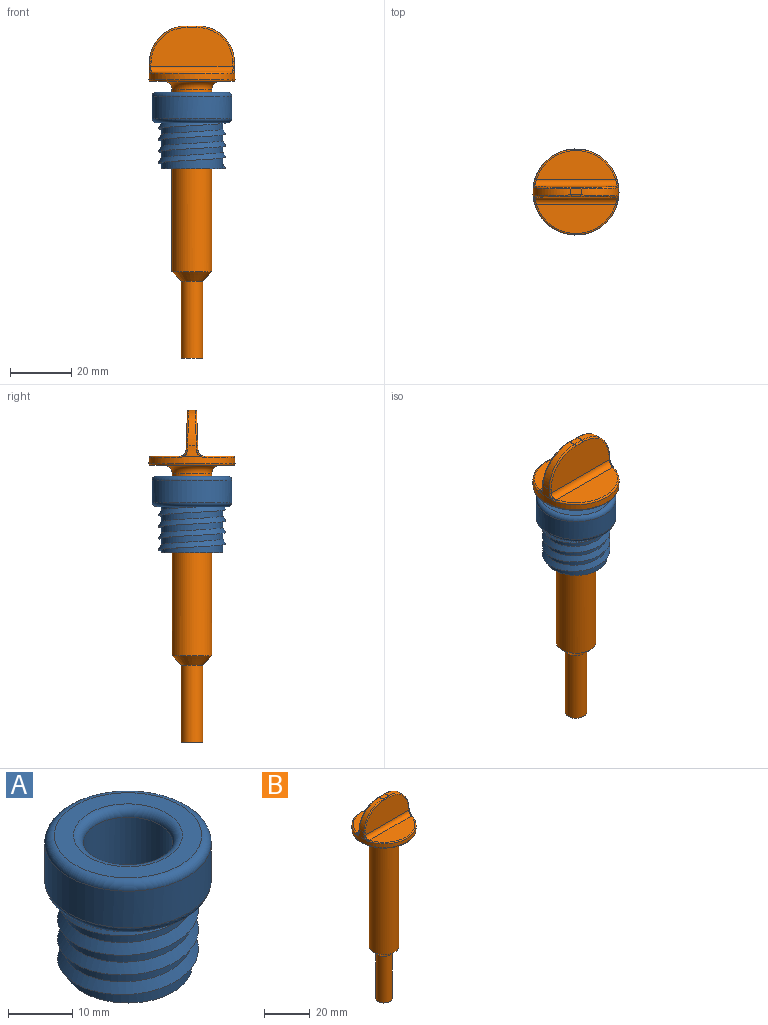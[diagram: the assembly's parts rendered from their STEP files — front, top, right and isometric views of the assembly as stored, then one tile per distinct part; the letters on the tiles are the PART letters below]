
ASSEMBLY  parts=2 mates=1
PART A: 12 faces, bbox 28.8x28.8x25.7 mm
  f0: plane 20x20mm, normal (0,0,-1), area 160.2mm2, adj f1,f5
  f1: cylinder r=10mm len=20mm, axis (0,0,-1), area 544.8mm2, adj f0,f2,f6,f7,f8
  f2: plane 23.71x23.71mm, normal (0,0,-1), area 86.3mm2, adj f1,f7,f8,f10
  f3: cylinder r=13mm len=26mm, axis (0,0,-1), area 571.8mm2, adj f10,f11
  f4: plane 23x23mm, normal (0,0,1), area 188.5mm2, adj f9,f11
  f5: cylinder r=7mm len=23.5mm, axis (0,0,1), area 1033.6mm2, adj f0,f9
  f6: plane 1.73x1mm, normal (0,-1,0), area 0.9mm2, adj f1,f7,f8
  f7: bspline ~25.4x22mm, area 264.5mm2, adj f1,f2,f6,f8
  f8: bspline ~25.4x22mm, area 498.6mm2, adj f1,f2,f6,f7
  f9: torus R=8.5mm, axis (0,0,-1), area 111.7mm2, adj f4,f5
  f10: torus R=11.5mm, axis (0,0,1), area 184.4mm2, adj f2,f3
  f11: torus R=11.5mm, axis (0,0,-1), area 184.4mm2, adj f3,f4
PART B: 39 faces, bbox 30.3x30.3x108 mm
  f0: plane 25.83x9.57mm, normal (0,0,1), area 181.7mm2, adj f17,f23
  f1: cylinder r=6.5mm len=59.5mm, axis (0,0,-1), area 2430mm2, adj f7,f8
  f2: cylinder r=14mm len=28mm, axis (0,0,-1), area 182.6mm2, adj f10,f12,f21,f23,f25,f31,f33,f35
  f3: plane 25.83x9.57mm, normal (0,0,1), area 181.7mm2, adj f16,f33
  f4: plane 27x27mm, normal (0,0,-1), area 318.1mm2, adj f8,f38
  f5: cylinder r=3.5mm len=25mm, axis (0,0,-1), area 549.8mm2, adj f6,f7
  f6: plane 7x7mm, normal (0,0,-1), area 38.5mm2, adj f5
  f7: cone r=6.5mm half-angle=45deg, axis (0,0,1), area 133.3mm2, adj f1,f5
  f8: torus R=9mm, axis (0,0,1), area 182.8mm2, adj f1,f4
  f9: plane 26.71x12.59mm, normal (0,1,0.03), area 278.8mm2, adj f17,f18,f20,f22,f24,f26
  f10: cone r=14mm half-angle=2deg, axis (0,0,-1), area 11.4mm2, adj f2,f14,f18,f19,f21,f35,f36,f37
  f11: plane 26.71x12.59mm, normal (0,-1,0.03), area 278.8mm2, adj f16,f28,f30,f32,f34,f36
  f12: cone r=14mm half-angle=2deg, axis (0,0,-1), area 11.4mm2, adj f2,f15,f25,f26,f27,f28,f29,f31
  f13: plane 3.78x1.99mm, normal (0,0,1), area 7.1mm2, adj f14,f15,f22,f32
  f14: torus R=1.89mm, axis (0,0,1), area 43.4mm2, adj f10,f13,f20,f34
  f15: torus R=1.89mm, axis (0,0,1), area 43.4mm2, adj f12,f13,f24,f30
  f16: cylinder r=2mm len=26.71mm, axis (-1,0,0), area 81.2mm2, adj f3,f11,f29,f31,f35,f37
  f17: cylinder r=2mm len=26.71mm, axis (-1,0,0), area 81.2mm2, adj f0,f9,f19,f21,f25,f27
  f18: bspline ~7.46x0.73mm, area 1.1mm2, adj f9,f10,f19,f20
  f19: bspline ~2.62x1.48mm, area 1.4mm2, adj f10,f17,f18,f21
  f20: bspline ~12.93x12.86mm, area 13.5mm2, adj f9,f14,f18,f22
  f21: bspline ~2.35x1.08mm, area 1.1mm2, adj f2,f10,f17,f19,f23
  f22: cylinder r=0.5mm len=3.21mm, axis (1,0,0), area 2.5mm2, adj f9,f13,f20,f24
  f23: torus R=13.5mm, axis (0,0,1), area 27.7mm2, adj f0,f2,f21,f25
  f24: bspline ~12.93x12.79mm, area 13.5mm2, adj f9,f15,f22,f26
  f25: bspline ~2.35x1.08mm, area 1.1mm2, adj f2,f12,f17,f23,f27
  f26: bspline ~7.46x0.73mm, area 1.1mm2, adj f9,f12,f24,f27
  f27: bspline ~2.2x1.48mm, area 1.4mm2, adj f12,f17,f25,f26
  f28: bspline ~5.22x0.66mm, area 1.1mm2, adj f11,f12,f29,f30
  f29: bspline ~2.62x1.48mm, area 1.4mm2, adj f12,f16,f28,f31
  f30: bspline ~12.93x12.79mm, area 13.5mm2, adj f11,f15,f28,f32
  f31: bspline ~2.35x1.08mm, area 1.1mm2, adj f2,f12,f16,f29,f33
  f32: cylinder r=0.5mm len=3.21mm, axis (1,0,0), area 2.5mm2, adj f11,f13,f30,f34
  f33: torus R=13.5mm, axis (0,0,1), area 27.7mm2, adj f2,f3,f31,f35
  f34: bspline ~12.93x12.86mm, area 13.5mm2, adj f11,f14,f32,f36
  f35: bspline ~2.35x1.08mm, area 1.1mm2, adj f2,f10,f16,f33,f37
  f36: bspline ~5.22x0.66mm, area 1.1mm2, adj f10,f11,f34,f37
  f37: bspline ~2.2x1.48mm, area 1.4mm2, adj f10,f16,f35,f36
  f38: torus R=13.5mm, axis (0,0,1), area 68.2mm2, adj f2,f4
PLACE A at identity fixed
PLACE B t=(0,0,-61.53)mm
MATE slider B.f1 <-> A.f5  axis (0,0,-1) through (0,0,-3.78)mm
